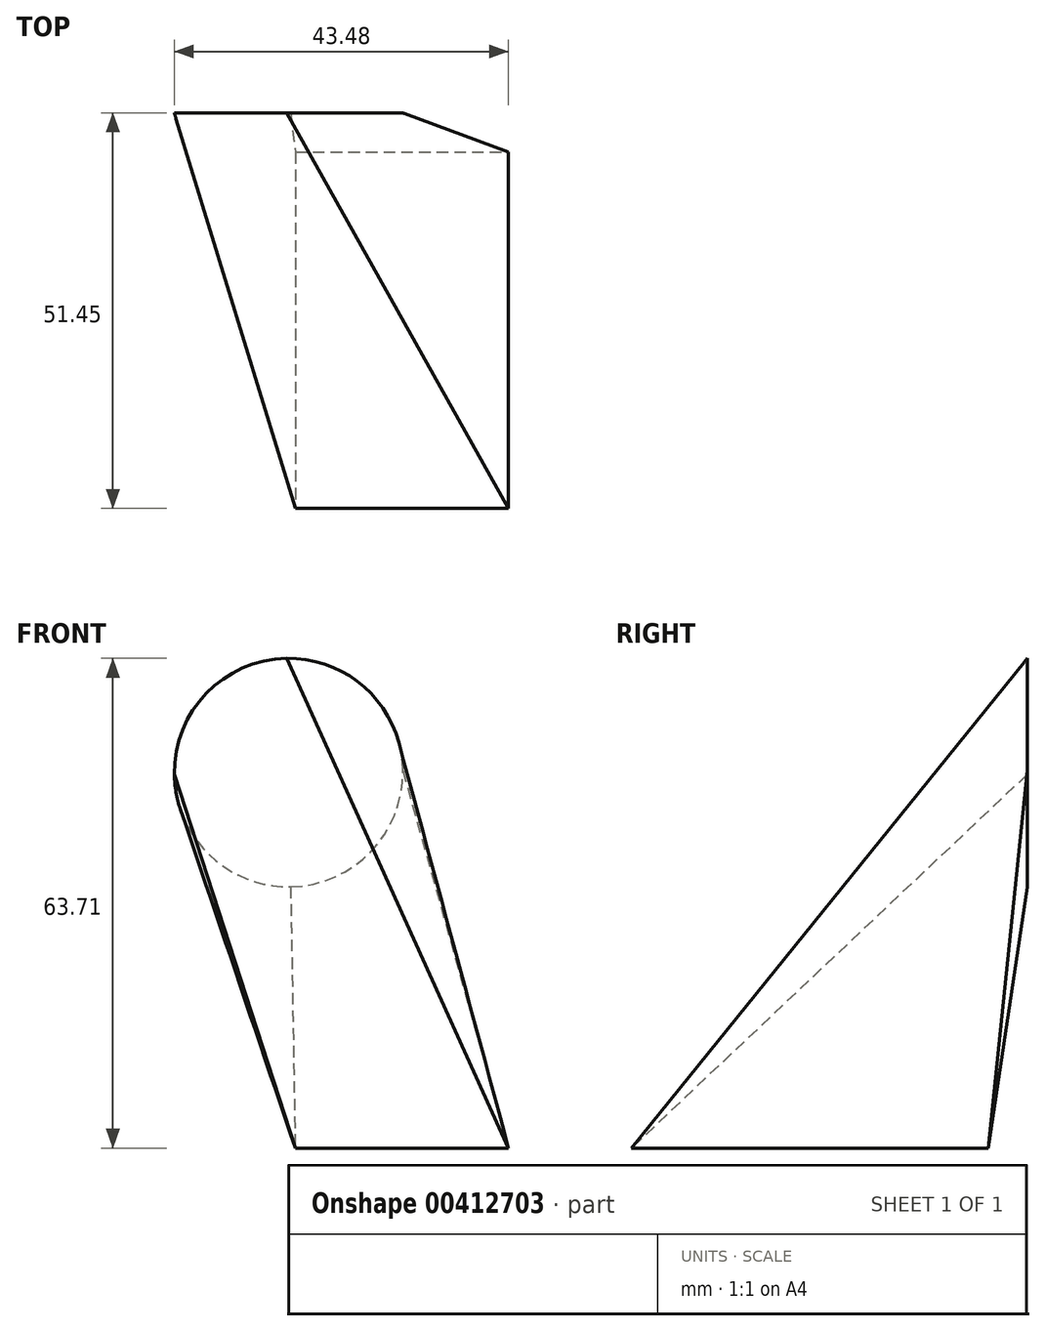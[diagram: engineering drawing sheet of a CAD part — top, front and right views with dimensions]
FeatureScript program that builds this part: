
annotation { "Feature Type Name" : "Feature", "Feature Type Description" : "" }
export const myFeature = defineFeature(function(context is Context, id is Id, definition is map)
    precondition{}
    {
        {
            var Q0;
            Q0=qCreatedBy(makeId("Top.planeOp"),FACE);
            var sketch = newSketch(context, id + "F0", { "sketchPlane" : qUnion([Q0])});
            skLineSegment(sketch, "E0.bottom", {"start": v(-55.8, -5.08) * mm, "end": v(-28.04, -5.08) * mm});
            skLineSegment(sketch, "E0.top", {"start": v(-55.8, -51.45) * mm, "end": v(-28.04, -51.45) * mm});
            skLineSegment(sketch, "E0.left", {"start": v(-55.8, -5.08) * mm, "end": v(-55.8, -51.45) * mm});
            skLineSegment(sketch, "E0.right", {"start": v(-28.04, -5.08) * mm, "end": v(-28.04, -51.45) * mm});
            skSolve(sketch);
        }
        {
            var Q0;
            Q0=qCreatedBy(makeId("Front.planeOp"),FACE);
            var sketch = newSketch(context, id + "F1", { "sketchPlane" : qUnion([Q0])});
            skCircle(sketch, "E1", {"center": v(-56.66, 48.85) * mm, "radius": 14.86 * mm});
            skSolve(sketch);
        }
        {
            var Q0;
            Q0 = qSketchRegion(id + "F1", true);
            var Q1;
            Q1 = qSketchRegion(id + "F0", true);
            loft(context, id + "F2", {"sheetProfilesArray" : [{ "sheetProfileEntities" : qUnion([Q0]) }, { "sheetProfileEntities" : qUnion([Q1]) }]});
        }
    });
